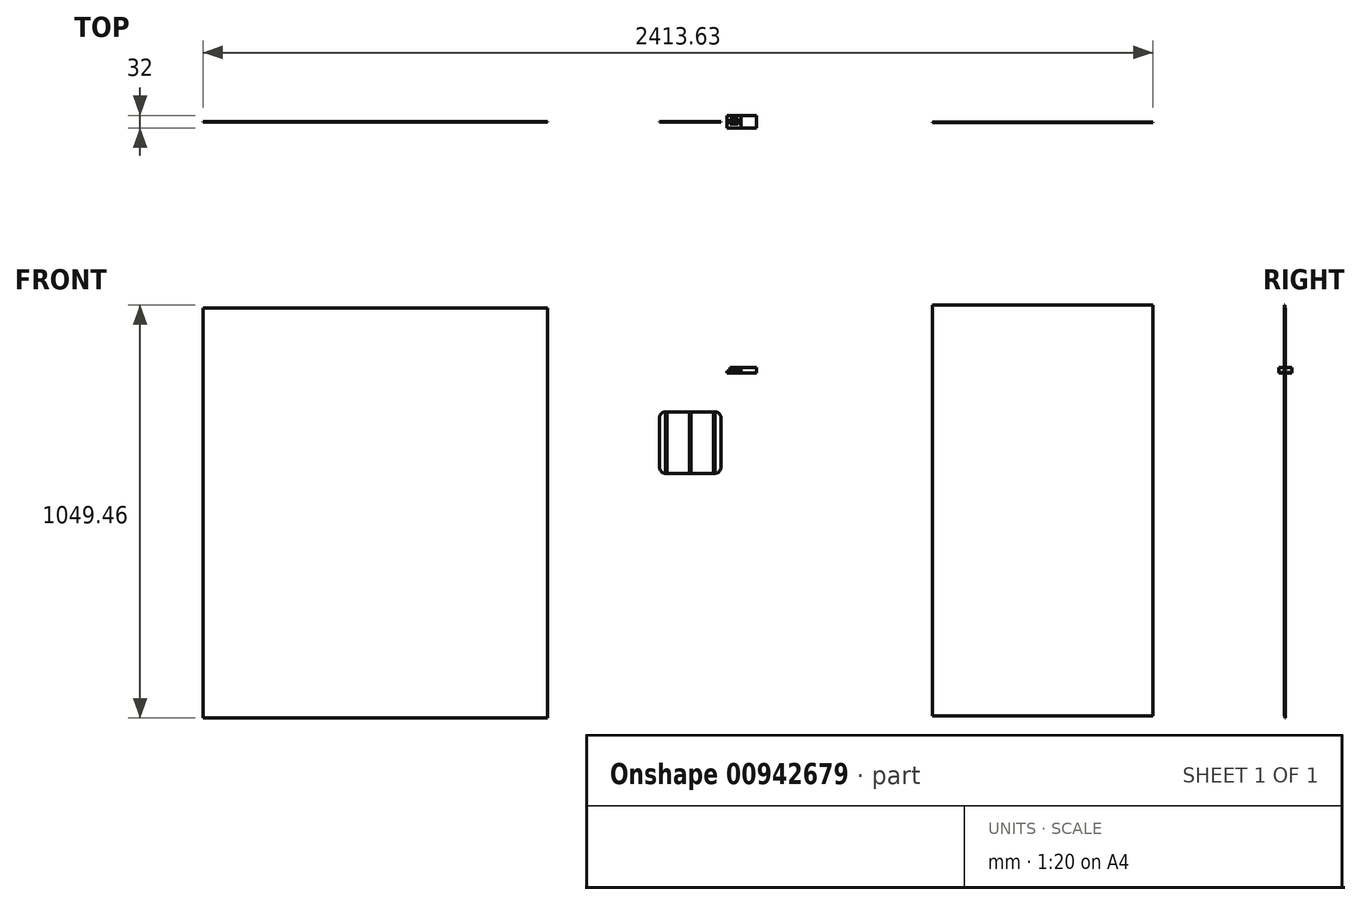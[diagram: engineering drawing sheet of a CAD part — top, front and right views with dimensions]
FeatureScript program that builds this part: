
annotation { "Feature Type Name" : "Feature", "Feature Type Description" : "" }
export const myFeature = defineFeature(function(context is Context, id is Id, definition is map)
    precondition{}
    {
        {
            var Q0;
            Q0=qCreatedBy(makeId("Front.planeOp"),FACE);
            var sketch = newSketch(context, id + "F0", { "sketchPlane" : qUnion([Q0])});
            skLineSegment(sketch, "E0.bottom", {"start": v(766.3, 681.77) * mm, "end": v(892.3, 681.77) * mm});
            skLineSegment(sketch, "E0.top", {"start": v(766.3, 525.77) * mm, "end": v(892.3, 525.77) * mm});
            skLineSegment(sketch, "E0.left", {"start": v(751.3, 666.77) * mm, "end": v(751.3, 540.77) * mm});
            skLineSegment(sketch, "E0.right", {"start": v(907.3, 666.77) * mm, "end": v(907.3, 540.77) * mm});
            skPoint(sketch, "E1.visualSharp", {"position": v(751.3, 681.77) * mm});
            skArc(sketch, "E1.filletArc", {"start": v(766.3, 681.77) * mm, "mid": v(755.7, 677.38) * mm, "end": v(751.3, 666.77) * mm});
            skPoint(sketch, "E2.visualSharp", {"position": v(907.3, 681.77) * mm});
            skArc(sketch, "E2.filletArc", {"start": v(907.3, 666.77) * mm, "mid": v(902.9, 677.38) * mm, "end": v(892.3, 681.77) * mm});
            skPoint(sketch, "E3.visualSharp", {"position": v(907.3, 525.77) * mm});
            skArc(sketch, "E3.filletArc", {"start": v(892.3, 525.77) * mm, "mid": v(902.9, 530.16) * mm, "end": v(907.3, 540.77) * mm});
            skPoint(sketch, "E4.visualSharp", {"position": v(751.3, 525.77) * mm});
            skArc(sketch, "E4.filletArc", {"start": v(751.3, 540.77) * mm, "mid": v(755.7, 530.16) * mm, "end": v(766.3, 525.77) * mm});
            skLineSegment(sketch, "E5.bottom", {"start": v(3038.85, 81858.35) * mm, "end": v(2869.38, 81858.35) * mm});
            skLineSegment(sketch, "E5.top", {"start": v(3038.85, 72650.5) * mm, "end": v(2869.38, 72650.5) * mm});
            skLineSegment(sketch, "E5.left", {"start": v(3038.85, 81858.35) * mm, "end": v(3038.85, 72650.5) * mm});
            skLineSegment(sketch, "E5.right", {"start": v(2869.38, 81858.35) * mm, "end": v(2869.38, 72650.5) * mm});
            skSolve(sketch);
        }
        {
            var Q0;
            Q0=makeQuery(id+"F0.imprint","IMPRINT",FACE,{"disambiguationData":[TD([[makeQuery(id+"F0.imprint","IMPRINT",EDGE,{"derivedFrom":sQuery(id+"F0.wireOp",EDGE,"E0.bottom")}),-1.0]])]});
            extrude(context, id + "F1", {"entities" : qUnion([Q0]), "depth" : 1 * mm, "offsetDistance" : 25 * mm});
        }
        {
            var Q0;
            Q0=makeQuery(id+"F1.opExtrude","CAP_FACE",FACE,{"disambiguationData":[OSD([sQuery(id+"F0.wireOp",EDGE,"E0.bottom"),sQuery(id+"F0.wireOp",EDGE,"E0.top"),sQuery(id+"F0.wireOp",EDGE,"E0.left"),sQuery(id+"F0.wireOp",EDGE,"E0.right"),sQuery(id+"F0.wireOp",EDGE,"E1.filletArc"),sQuery(id+"F0.wireOp",EDGE,"E2.filletArc"),sQuery(id+"F0.wireOp",EDGE,"E3.filletArc"),sQuery(id+"F0.wireOp",EDGE,"E4.filletArc")])],"isStart":false});
            var sketch = newSketch(context, id + "F2", { "sketchPlane" : qUnion([Q0])});
            skLineSegment(sketch, "E6.bottom", {"start": v(1068.35, 691.33) * mm, "end": v(1072.64, 691.33) * mm});
            skLineSegment(sketch, "E6.top", {"start": v(1068.35, 535.33) * mm, "end": v(1072.64, 535.33) * mm});
            skLineSegment(sketch, "E6.left", {"start": v(1068.35, 691.33) * mm, "end": v(1068.35, 535.33) * mm});
            skLineSegment(sketch, "E6.right", {"start": v(1072.64, 691.33) * mm, "end": v(1072.64, 535.33) * mm});
            skLineSegment(sketch, "E7.bottom", {"start": v(1040.3, 699.13) * mm, "end": v(1044.6, 699.13) * mm});
            skLineSegment(sketch, "E7.top", {"start": v(1040.3, 543.13) * mm, "end": v(1044.6, 543.13) * mm});
            skLineSegment(sketch, "E7.left", {"start": v(1040.3, 699.13) * mm, "end": v(1040.3, 543.13) * mm});
            skLineSegment(sketch, "E7.right", {"start": v(1044.6, 699.13) * mm, "end": v(1044.6, 543.13) * mm});
            skLineSegment(sketch, "E8.bottom", {"start": v(997.94, 678.37) * mm, "end": v(1002.23, 678.37) * mm});
            skLineSegment(sketch, "E8.top", {"start": v(997.94, 522.37) * mm, "end": v(1002.23, 522.37) * mm});
            skLineSegment(sketch, "E8.left", {"start": v(997.94, 678.37) * mm, "end": v(997.94, 522.37) * mm});
            skLineSegment(sketch, "E8.right", {"start": v(1002.23, 678.37) * mm, "end": v(1002.23, 522.37) * mm});
            skSolve(sketch);
        }
        {
            var Q0;
            Q0=makeQuery(id+"F2.imprint","IMPRINT",FACE,{"disambiguationData":[TD([[makeQuery(id+"F2.imprint","IMPRINT",EDGE,{"derivedFrom":sQuery(id+"F2.wireOp",EDGE,"E6.bottom")}),-1.0]])]});
            var Q1;
            Q1=makeQuery(id+"F2.imprint","IMPRINT",FACE,{"disambiguationData":[TD([[makeQuery(id+"F2.imprint","IMPRINT",EDGE,{"derivedFrom":sQuery(id+"F2.wireOp",EDGE,"E7.bottom")}),-1.0]])]});
            var Q2;
            Q2=makeQuery(id+"F2.imprint","IMPRINT",FACE,{"disambiguationData":[TD([[makeQuery(id+"F2.imprint","IMPRINT",EDGE,{"derivedFrom":sQuery(id+"F2.wireOp",EDGE,"E8.bottom")}),-1.0]])]});
            extrude(context, id + "F3", {"entities" : qUnion([Q0, Q1, Q2]), "depth" : 0.5 * mm, "offsetDistance" : 25 * mm});
        }
        {
            var Q0;
            Q0=makeQuery(id+"F3.opExtrude","SWEPT_BODY",BODY,{"disambiguationData":[OSD([sQuery(id+"F2.wireOp",EDGE,"E8.bottom"),sQuery(id+"F2.wireOp",EDGE,"E8.top"),sQuery(id+"F2.wireOp",EDGE,"E8.left"),sQuery(id+"F2.wireOp",EDGE,"E8.right")])]});
            transform(context, id + "F4", {"entities" : qUnion([Q0]), "transformType" : TransformType.TRANSLATION_3D, "dx" : -232.8 * mm, "dy" : 0 * mm, "dz" : 3.3 * mm, "makeCopy" : false});
        }
        {
            var Q0;
            Q0=makeQuery(id+"F3.opExtrude","SWEPT_BODY",BODY,{"disambiguationData":[OSD([sQuery(id+"F2.wireOp",EDGE,"E8.bottom"),sQuery(id+"F2.wireOp",EDGE,"E8.top"),sQuery(id+"F2.wireOp",EDGE,"E8.left"),sQuery(id+"F2.wireOp",EDGE,"E8.right")])]});
            transform(context, id + "F5", {"entities" : qUnion([Q0]), "transformType" : TransformType.TRANSLATION_3D, "dx" : 6E-4000 * mm, "dy" : 0 * mm, "dz" : 0 * mm, "makeCopy" : false});
        }
        {
            var Q0;
            Q0=makeQuery(id+"F3.opExtrude","SWEPT_BODY",BODY,{"disambiguationData":[OSD([sQuery(id+"F2.wireOp",EDGE,"E8.bottom"),sQuery(id+"F2.wireOp",EDGE,"E8.top"),sQuery(id+"F2.wireOp",EDGE,"E8.left"),sQuery(id+"F2.wireOp",EDGE,"E8.right")])]});
            var Q1;
            Q1=makeQuery(id+"F3.opExtrude","CAP_VERTEX",VERTEX,{"disambiguationData":[OSD([sQuery(id+"F2.wireOp",EDGE,"E8.top"),sQuery(id+"F2.wireOp",EDGE,"E8.left")])],"isStart":false});
            var Q2;
            Q2=makeQuery(id+"F1.opExtrude","CAP_EDGE",EDGE,{"disambiguationData":[OSD([sQuery(id+"F0.wireOp",EDGE,"E0.top")])],"isStart":false});
            transform(context, id + "F6", {"entities" : qUnion([Q0]), "transformType" : TransformType.TRANSLATION_ENTITY, "oppositeDirectionEntity" : false, "transformLine" : qUnion([Q1, Q2]), "makeCopy" : false});
        }
        {
            var Q0;
            Q0=makeQuery(id+"F3.opExtrude","SWEPT_BODY",BODY,{"disambiguationData":[OSD([sQuery(id+"F2.wireOp",EDGE,"E8.bottom"),sQuery(id+"F2.wireOp",EDGE,"E8.top"),sQuery(id+"F2.wireOp",EDGE,"E8.left"),sQuery(id+"F2.wireOp",EDGE,"E8.right")])]});
            var Q1;
            Q1=makeQuery(id+"F3.opExtrude","CAP_VERTEX",VERTEX,{"disambiguationData":[OSD([sQuery(id+"F2.wireOp",EDGE,"E8.bottom"),sQuery(id+"F2.wireOp",EDGE,"E8.right")])],"isStart":true});
            var Q2;
            Q2=makeQuery(id+"F1.opExtrude","CAP_VERTEX",VERTEX,{"disambiguationData":[OSD([sQuery(id+"F0.wireOp",EDGE,"E0.bottom"),sQuery(id+"F0.wireOp",EDGE,"E2.filletArc")])],"isStart":false});
            transform(context, id + "F7", {"entities" : qUnion([Q0]), "transformType" : TransformType.TRANSLATION_ENTITY, "oppositeDirectionEntity" : false, "transformLine" : qUnion([Q1, Q2]), "makeCopy" : false});
        }
        {
            var Q0;
            Q0=makeQuery(id+"F3.opExtrude","SWEPT_BODY",BODY,{"disambiguationData":[OSD([sQuery(id+"F2.wireOp",EDGE,"E7.bottom"),sQuery(id+"F2.wireOp",EDGE,"E7.top"),sQuery(id+"F2.wireOp",EDGE,"E7.left"),sQuery(id+"F2.wireOp",EDGE,"E7.right")])]});
            var Q1;
            Q1=sQuery(id+"F2.wireOp",VERTEX,"E7.bottom.start");
            var Q2;
            Q2=makeQuery(id+"F1.opExtrude","CAP_VERTEX",VERTEX,{"disambiguationData":[OSD([sQuery(id+"F0.wireOp",EDGE,"E0.bottom"),sQuery(id+"F0.wireOp",EDGE,"E1.filletArc")])],"isStart":false});
            transform(context, id + "F8", {"entities" : qUnion([Q0]), "transformType" : TransformType.TRANSLATION_ENTITY, "oppositeDirectionEntity" : false, "transformLine" : qUnion([Q1, Q2]), "makeCopy" : false});
        }
        {
            var Q0;
            Q0=sQuery(id+"F2.wireOp",EDGE,"E6.bottom");
            cPoint(context, id + "F9", {"entities" : qUnion([Q0]), "parameter" : 0.5});
        }
        {
            var Q0;
            Q0=makeQuery(id+"F1.opExtrude","CAP_EDGE",EDGE,{"disambiguationData":[OSD([sQuery(id+"F0.wireOp",EDGE,"E0.bottom")])],"isStart":false});
            cPoint(context, id + "F10", {"entities" : qUnion([Q0]), "parameter" : 0.5});
        }
        {
            var Q0;
            Q0=makeQuery(id+"F3.opExtrude","SWEPT_BODY",BODY,{"disambiguationData":[OSD([sQuery(id+"F2.wireOp",EDGE,"E6.bottom"),sQuery(id+"F2.wireOp",EDGE,"E6.top"),sQuery(id+"F2.wireOp",EDGE,"E6.left"),sQuery(id+"F2.wireOp",EDGE,"E6.right")])]});
            var Q1;
            Q1=qCreatedBy(id+"F9",VERTEX);
            var Q2;
            Q2=qCreatedBy(id+"F10",VERTEX);
            transform(context, id + "F11", {"entities" : qUnion([Q0]), "transformType" : TransformType.TRANSLATION_ENTITY, "oppositeDirectionEntity" : false, "transformLine" : qUnion([Q1, Q2]), "makeCopy" : false});
        }
        {
            var Q0;
            Q0=qCreatedBy(makeId("Front.planeOp"),FACE);
            var sketch = newSketch(context, id + "F12", { "sketchPlane" : qUnion([Q0])});
            skLineSegment(sketch, "E9.right", {"start": v(997.16, 786.05) * mm, "end": v(997.16, 780.2) * mm});
            skPoint(sketch, "E10.oppositeSnap0", {"position": v(958.16, 786.05) * mm});
            skLineSegment(sketch, "E10.bottom", {"start": v(997.16, 786.05) * mm, "end": v(958.16, 786.05) * mm});
            skLineSegment(sketch, "E10.top", {"start": v(997.16, 794.2) * mm, "end": v(958.16, 794.2) * mm});
            skLineSegment(sketch, "E10.left", {"start": v(997.16, 786.05) * mm, "end": v(997.16, 794.2) * mm});
            skLineSegment(sketch, "E10.right", {"start": v(958.16, 786.05) * mm, "end": v(958.16, 794.2) * mm});
            skLineSegment(sketch, "E11.bottom", {"start": v(958.16, 790.13) * mm, "end": v(930.77, 790.13) * mm});
            skLineSegment(sketch, "E11.top", {"start": v(958.16, 786.05) * mm, "end": v(930.77, 786.05) * mm});
            skLineSegment(sketch, "E11.left", {"start": v(958.16, 790.13) * mm, "end": v(958.16, 786.05) * mm});
            skLineSegment(sketch, "E11.right", {"start": v(930.77, 790.13) * mm, "end": v(930.77, 786.05) * mm});
            skLineSegment(sketch, "E12", {"start": v(997.16, 780.2) * mm, "end": v(923.16, 780.2) * mm});
            skLineSegment(sketch, "E13", {"start": v(923.16, 780.2) * mm, "end": v(923.16, 786.05) * mm});
            skLineSegment(sketch, "E14", {"start": v(923.16, 786.05) * mm, "end": v(930.77, 786.05) * mm});
            skSolve(sketch);
        }
        {
            var Q0;
            Q0=makeQuery(id+"F12.imprint","IMPRINT",FACE,{"disambiguationData":[TD([[makeQuery(id+"F12.imprint","IMPRINT",EDGE,{"derivedFrom":sQuery(id+"F12.wireOp",EDGE,"E10.bottom")}),-1.0]])]});
            var Q1;
            Q1=makeQuery(id+"F12.imprint","IMPRINT",FACE,{"disambiguationData":[TD([[makeQuery(id+"F12.imprint","IMPRINT",EDGE,{"derivedFrom":sQuery(id+"F12.wireOp",EDGE,"E9.bottom")}),-1.0]])]});
            var Q2;
            Q2=makeQuery(id+"F12.imprint","IMPRINT",FACE,{"disambiguationData":[TD([[makeQuery(id+"F12.imprint","IMPRINT",EDGE,{"derivedFrom":sQuery(id+"F12.wireOp",EDGE,"E9.right")}),-1.0]])]});
            extrude(context, id + "F13", {"entities" : qUnion([Q0, Q1, Q2]), "endBound" : BoundingType.SYMMETRIC, "depth" : 32 * mm, "offsetDistance" : 25 * mm});
        }
        {
            var Q0;
            Q0=makeQuery(id+"F12.imprint","IMPRINT",FACE,{"disambiguationData":[TD([[makeQuery(id+"F12.imprint","IMPRINT",EDGE,{"derivedFrom":sQuery(id+"F12.wireOp",EDGE,"E11.bottom")}),1.0]])]});
            var Q1;
            Q1=sQuery(id+"F12.wireOp",EDGE,"E11.bottom");
            revolve(context, id + "F14", {"surfaceOperationType" : NewSurfaceOperationType.NEW, "entities" : qUnion([Q0]), "axis" : qUnion([Q1]), "revolveType" : RevolveType.ONE_DIRECTION, "angle" : 360 * degree});
        }
        {
            var Q0;
            Q0=makeQuery(id+"F14.opRevolve","SWEPT_FACE",FACE,{"disambiguationData":[OSD([sQuery(id+"F12.wireOp",EDGE,"E11.right")])]});
            var sketch = newSketch(context, id + "F15", { "sketchPlane" : qUnion([Q0])});
            skCircle(sketch, "E15", {"center": v(0, 790.13) * mm, "radius": 7.66 * mm});
            skSolve(sketch);
        }
        {
            var Q0;
            Q0=makeQuery(id+"F15.imprint","IMPRINT",FACE,{"disambiguationData":[TD([[makeQuery(id+"F15.imprint","IMPRINT",EDGE,{"derivedFrom":sQuery(id+"F15.wireOp",EDGE,"E15")}),1.0]])]});
            extrude(context, id + "F16", {"entities" : qUnion([Q0]), "operationType" : NewBodyOperationType.REMOVE, "depth" : -20 * mm, "offsetDistance" : 25 * mm});
        }
        {
            var Q0;
            Q0=qCreatedBy(makeId("Front.planeOp"),FACE);
            var sketch = newSketch(context, id + "F17", { "sketchPlane" : qUnion([Q0])});
            skLineSegment(sketch, "E16.bottom", {"start": v(-408.46, 945.17) * mm, "end": v(466.54, 945.17) * mm});
            skLineSegment(sketch, "E16.top", {"start": v(-408.46, -96.23) * mm, "end": v(466.54, -96.23) * mm});
            skLineSegment(sketch, "E16.left", {"start": v(-408.46, 945.17) * mm, "end": v(-408.46, -96.23) * mm});
            skLineSegment(sketch, "E16.right", {"start": v(466.54, 945.17) * mm, "end": v(466.54, -96.23) * mm});
            skSolve(sketch);
        }
        {
            var Q0;
            Q0=makeQuery(id+"F17.imprint","IMPRINT",FACE,{"disambiguationData":[TD([[makeQuery(id+"F17.imprint","IMPRINT",EDGE,{"derivedFrom":sQuery(id+"F17.wireOp",EDGE,"E16.bottom")}),-1.0]])]});
            extrude(context, id + "F18", {"entities" : qUnion([Q0]), "depth" : 1 * mm, "offsetDistance" : 25.4 * mm});
        }
        {
            var Q0;
            Q0=makeQuery(id+"F18.opExtrude","CAP_FACE",FACE,{"disambiguationData":[OSD([sQuery(id+"F17.wireOp",EDGE,"E16.bottom"),sQuery(id+"F17.wireOp",EDGE,"E16.top"),sQuery(id+"F17.wireOp",EDGE,"E16.left"),sQuery(id+"F17.wireOp",EDGE,"E16.right")])],"isStart":false});
            var sketch = newSketch(context, id + "F19", { "sketchPlane" : qUnion([Q0])});
            skLineSegment(sketch, "E17.bottom", {"start": v(1445.17, 953.23) * mm, "end": v(2005.17, 953.23) * mm});
            skLineSegment(sketch, "E17.top", {"start": v(1445.17, -90.77) * mm, "end": v(2005.17, -90.77) * mm});
            skLineSegment(sketch, "E17.left", {"start": v(1445.17, 953.23) * mm, "end": v(1445.17, -90.77) * mm});
            skLineSegment(sketch, "E17.right", {"start": v(2005.17, 953.23) * mm, "end": v(2005.17, -90.77) * mm});
            skSolve(sketch);
        }
        {
            var Q0;
            Q0=makeQuery(id+"F19.imprint","IMPRINT",FACE,{"disambiguationData":[TD([[makeQuery(id+"F19.imprint","IMPRINT",EDGE,{"derivedFrom":sQuery(id+"F19.wireOp",EDGE,"E17.bottom")}),-1.0]])]});
            extrude(context, id + "F20", {"entities" : qUnion([Q0]), "depth" : 1 * mm, "offsetDistance" : 25.4 * mm});
        }
    });
